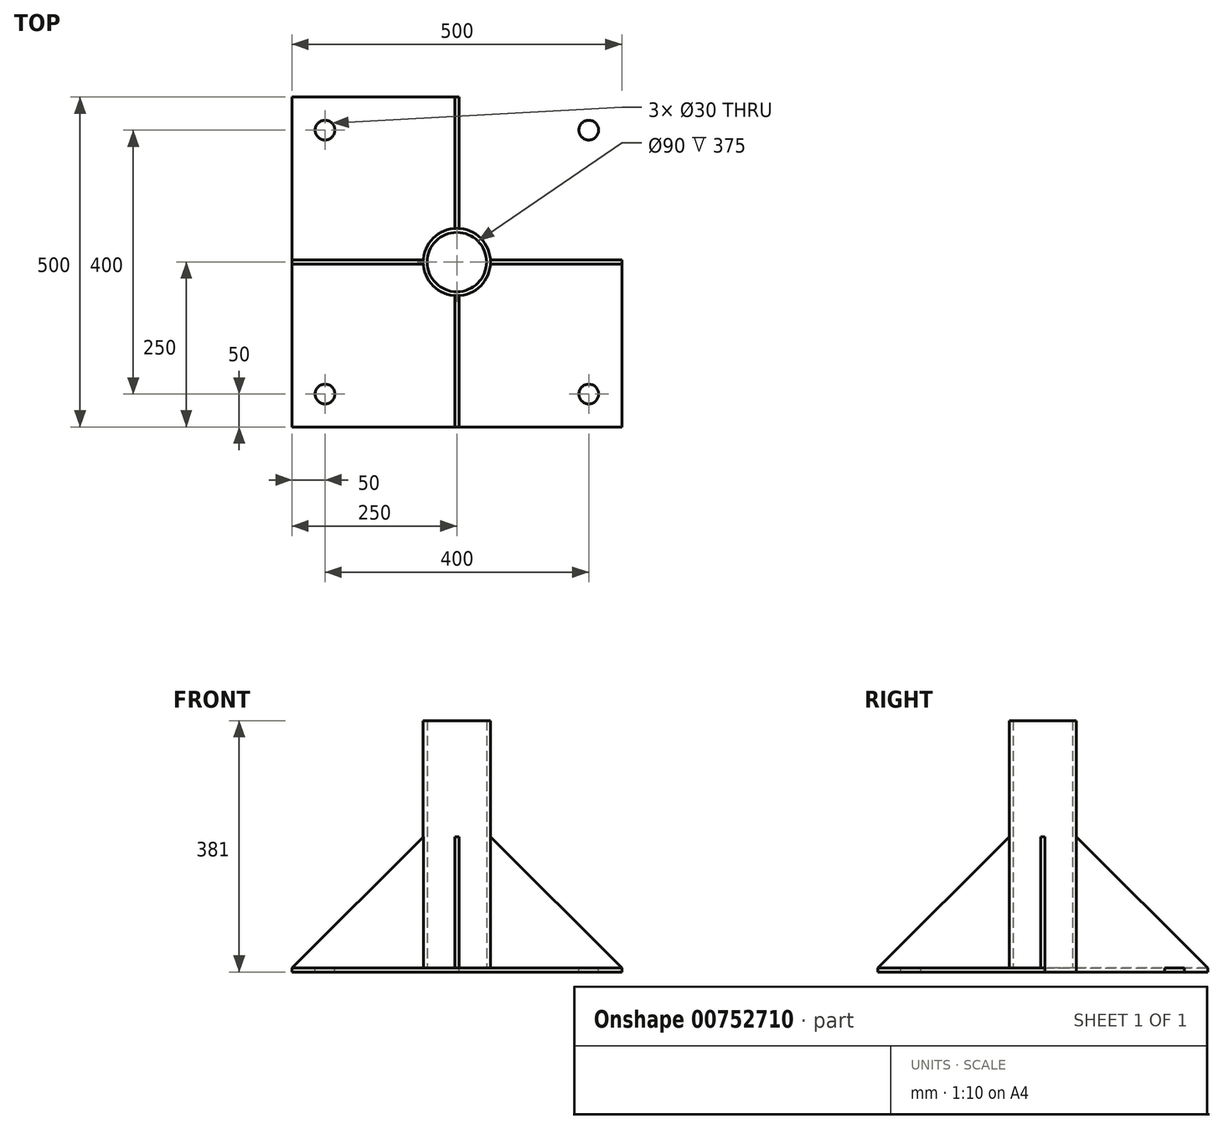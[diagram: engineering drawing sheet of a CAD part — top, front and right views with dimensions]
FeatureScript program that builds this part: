
annotation { "Feature Type Name" : "Feature", "Feature Type Description" : "" }
export const myFeature = defineFeature(function(context is Context, id is Id, definition is map)
    precondition{}
    {
        {
            var Q0;
            Q0=qCreatedBy(makeId("Top.planeOp"),FACE);
            var sketch = newSketch(context, id + "F0", { "sketchPlane" : qUnion([Q0])});
            skLineSegment(sketch, "E0.bottom", {"start": v(250, -250) * mm, "end": v(-250, -250) * mm});
            skLineSegment(sketch, "E0.top", {"start": v(250, 250) * mm, "end": v(-250, 250) * mm});
            skLineSegment(sketch, "E0.left", {"start": v(250, -250) * mm, "end": v(250, 250) * mm});
            skLineSegment(sketch, "E0.right", {"start": v(-250, -250) * mm, "end": v(-250, 250) * mm});
            skPoint(sketch, "E0.middle", {"position": v(0, 0) * mm});
            skSolve(sketch);
        }
        {
            var Q0;
            Q0=makeQuery(id+"F0.imprint","IMPRINT",FACE,{"disambiguationData":[TD([[makeQuery(id+"F0.imprint","IMPRINT",EDGE,{"derivedFrom":sQuery(id+"F0.wireOp",EDGE,"E0.bottom")}),-1.0]])]});
            extrude(context, id + "F1", {"entities" : qUnion([Q0]), "depth" : 6 * mm, "offsetDistance" : 25 * mm});
        }
        {
            var Q0;
            Q0=makeQuery(id+"F1.opExtrude","CAP_FACE",FACE,{"disambiguationData":[OSD([sQuery(id+"F0.wireOp",EDGE,"E0.bottom"),sQuery(id+"F0.wireOp",EDGE,"E0.top"),sQuery(id+"F0.wireOp",EDGE,"E0.left"),sQuery(id+"F0.wireOp",EDGE,"E0.right")])],"isStart":false});
            var sketch = newSketch(context, id + "F2", { "sketchPlane" : qUnion([Q0])});
            skCircle(sketch, "E1", {"center": v(0, 0) * mm, "radius": 45 * mm});
            skCircle(sketch, "E2", {"center": v(0, 0) * mm, "radius": 51 * mm});
            skLineSegment(sketch, "E3", {"start": v(250, 3) * mm, "end": v(50.91, 3) * mm});
            skLineSegment(sketch, "E4", {"start": v(250, -3) * mm, "end": v(50.91, -3) * mm});
            skLineSegment(sketch, "E5", {"start": v(-3, 250) * mm, "end": v(-3, 50.91) * mm});
            skLineSegment(sketch, "E6", {"start": v(3, 250) * mm, "end": v(3, 50.91) * mm});
            skLineSegment(sketch, "E7", {"start": v(3, -250) * mm, "end": v(3, -50.91) * mm});
            skLineSegment(sketch, "E8", {"start": v(-3, -250) * mm, "end": v(-3, -50.91) * mm});
            skLineSegment(sketch, "E9", {"start": v(-250, 3) * mm, "end": v(-50.91, 3) * mm});
            skLineSegment(sketch, "E10", {"start": v(-50.91, -3) * mm, "end": v(-250, -3) * mm});
            skCircle(sketch, "E11", {"center": v(200, 200) * mm, "radius": 15 * mm});
            skPoint(sketch, "E11.first.point", {"position": v(202.47, 214.8) * mm});
            skPoint(sketch, "E11.second.point", {"position": v(214.93, 198.54) * mm});
            skPoint(sketch, "E11.third.point", {"position": v(214.73, 197.19) * mm});
            skCircle(sketch, "E12", {"center": v(-200, 200) * mm, "radius": 15 * mm});
            skPoint(sketch, "E12.first.point", {"position": v(-187.4, 191.86) * mm});
            skPoint(sketch, "E12.second.point", {"position": v(-187.04, 207.55) * mm});
            skPoint(sketch, "E12.third.point", {"position": v(-185.27, 197.19) * mm});
            skCircle(sketch, "E13", {"center": v(-200, -200) * mm, "radius": 15 * mm});
            skPoint(sketch, "E13.first.point", {"position": v(-207.7, -212.87) * mm});
            skPoint(sketch, "E13.second.point", {"position": v(-194.3, -186.13) * mm});
            skPoint(sketch, "E13.third.point", {"position": v(-185.56, -204.06) * mm});
            skCircle(sketch, "E14", {"center": v(200, -200) * mm, "radius": 15 * mm});
            skPoint(sketch, "E14.first.point", {"position": v(186.75, -207.04) * mm});
            skPoint(sketch, "E14.second.point", {"position": v(214.73, -197.19) * mm});
            skPoint(sketch, "E14.third.point", {"position": v(193.26, -186.6) * mm});
            skSolve(sketch);
        }
        {
            var Q0;
            {var subQ0=sQuery(id+"F2.wireOp",EDGE,"E5");Q0=makeQuery(id+"F2.imprint","IMPRINT",FACE,{"disambiguationData":[TD([[makeQuery(id+"F2.imprint","IMPRINT",EDGE,{"derivedFrom":subQ0}),1.0]])]});}
            var Q1;
            {var subQ0=sQuery(id+"F2.wireOp",EDGE,"E3");Q1=makeQuery(id+"F2.imprint","IMPRINT",FACE,{"disambiguationData":[TD([[makeQuery(id+"F2.imprint","IMPRINT",EDGE,{"derivedFrom":subQ0}),1.0]])]});}
            var Q2;
            {var subQ0=sQuery(id+"F2.wireOp",EDGE,"E9");Q2=makeQuery(id+"F2.imprint","IMPRINT",FACE,{"disambiguationData":[TD([[makeQuery(id+"F2.imprint","IMPRINT",EDGE,{"derivedFrom":subQ0}),-1.0]])]});}
            var Q3;
            {var subQ0=sQuery(id+"F2.wireOp",EDGE,"E7");Q3=makeQuery(id+"F2.imprint","IMPRINT",FACE,{"disambiguationData":[TD([[makeQuery(id+"F2.imprint","IMPRINT",EDGE,{"derivedFrom":subQ0}),1.0]])]});}
            extrude(context, id + "F3", {"entities" : qUnion([Q0, Q1, Q2, Q3]), "operationType" : NewBodyOperationType.ADD, "depth" : 200.1 * mm, "offsetDistance" : 25 * mm});
        }
        {
            var Q0;
            Q0=makeQuery(id+"F3.opExtrude","SWEPT_FACE",FACE,{"disambiguationData":[OSD([sQuery(id+"F2.wireOp",EDGE,"E3")])]});
            var sketch = newSketch(context, id + "F4", { "sketchPlane" : qUnion([Q0])});
            skLineSegment(sketch, "E15", {"start": v(-250, 6) * mm, "end": v(-50.91, 205.09) * mm});
            skSolve(sketch);
        }
        {
            var Q0;
            {var subQ0=sQuery(id+"F4.wireOp",EDGE,"E15");Q0=makeQuery(id+"F4.imprint","IMPRINT",FACE,{"disambiguationData":[TD([[makeQuery(id+"F4.imprint","IMPRINT",EDGE,{"derivedFrom":subQ0}),1.0]])]});}
            extrude(context, id + "F5", {"entities" : qUnion([Q0]), "operationType" : NewBodyOperationType.REMOVE, "oppositeDirection" : true, "depth" : 25 * mm, "offsetDistance" : 25 * mm});
        }
        {
            var Q0;
            Q0=makeQuery(id+"F3.opExtrude","SWEPT_FACE",FACE,{"disambiguationData":[OSD([sQuery(id+"F2.wireOp",EDGE,"E7")])]});
            var sketch = newSketch(context, id + "F6", { "sketchPlane" : qUnion([Q0])});
            skLineSegment(sketch, "E16", {"start": v(-250, 6) * mm, "end": v(-50.91, 205.09) * mm});
            skSolve(sketch);
        }
        {
            var Q0;
            Q0=makeQuery(id+"F3.opExtrude","SWEPT_FACE",FACE,{"disambiguationData":[OSD([sQuery(id+"F2.wireOp",EDGE,"E5")])]});
            var sketch = newSketch(context, id + "F7", { "sketchPlane" : qUnion([Q0])});
            skLineSegment(sketch, "E17", {"start": v(-250, 6) * mm, "end": v(-50.91, 205.09) * mm});
            skSolve(sketch);
        }
        {
            var Q0;
            {var subQ0=sQuery(id+"F6.wireOp",EDGE,"E16");Q0=makeQuery(id+"F6.imprint","IMPRINT",FACE,{"disambiguationData":[TD([[makeQuery(id+"F6.imprint","IMPRINT",EDGE,{"derivedFrom":subQ0}),1.0]])]});}
            extrude(context, id + "F8", {"entities" : qUnion([Q0]), "operationType" : NewBodyOperationType.REMOVE, "oppositeDirection" : true, "depth" : 25 * mm, "offsetDistance" : 25 * mm});
        }
        {
            var Q0;
            {var subQ0=sQuery(id+"F7.wireOp",EDGE,"E17");Q0=makeQuery(id+"F7.imprint","IMPRINT",FACE,{"disambiguationData":[TD([[makeQuery(id+"F7.imprint","IMPRINT",EDGE,{"derivedFrom":subQ0}),1.0]])]});}
            extrude(context, id + "F9", {"entities" : qUnion([Q0]), "operationType" : NewBodyOperationType.REMOVE, "oppositeDirection" : true, "depth" : 25 * mm, "offsetDistance" : 25 * mm});
        }
        {
            var Q0;
            Q0=makeQuery(id+"F2.imprint","IMPRINT",FACE,{"disambiguationData":[TD([[makeQuery(id+"F2.imprint","IMPRINT",EDGE,{"derivedFrom":sQuery(id+"F2.wireOp",EDGE,"E13")}),1.0]])]});
            var Q1;
            Q1=makeQuery(id+"F2.imprint","IMPRINT",FACE,{"disambiguationData":[TD([[makeQuery(id+"F2.imprint","IMPRINT",EDGE,{"derivedFrom":sQuery(id+"F2.wireOp",EDGE,"E14")}),1.0]])]});
            var Q2;
            Q2=makeQuery(id+"F2.imprint","IMPRINT",FACE,{"disambiguationData":[TD([[makeQuery(id+"F2.imprint","IMPRINT",EDGE,{"derivedFrom":sQuery(id+"F2.wireOp",EDGE,"E11")}),-1.0]])]});
            var Q3;
            Q3=makeQuery(id+"F2.imprint","IMPRINT",FACE,{"disambiguationData":[TD([[makeQuery(id+"F2.imprint","IMPRINT",EDGE,{"derivedFrom":sQuery(id+"F2.wireOp",EDGE,"E12")}),1.0]])]});
            extrude(context, id + "F10", {"entities" : qUnion([Q0, Q1, Q2, Q3]), "operationType" : NewBodyOperationType.REMOVE, "oppositeDirection" : true, "depth" : 25 * mm, "offsetDistance" : 25 * mm});
        }
        {
            var Q0;
            Q0=makeQuery(id+"F3.opExtrude","SWEPT_FACE",FACE,{"disambiguationData":[OSD([sQuery(id+"F2.wireOp",EDGE,"E10")])]});
            var sketch = newSketch(context, id + "F11", { "sketchPlane" : qUnion([Q0])});
            skLineSegment(sketch, "E18", {"start": v(-250, 6) * mm, "end": v(-50.91, 205.09) * mm});
            skSolve(sketch);
        }
        {
            var Q0;
            {var subQ0=sQuery(id+"F11.wireOp",EDGE,"E18");Q0=makeQuery(id+"F11.imprint","IMPRINT",FACE,{"disambiguationData":[TD([[makeQuery(id+"F11.imprint","IMPRINT",EDGE,{"derivedFrom":subQ0}),1.0]])]});}
            extrude(context, id + "F12", {"entities" : qUnion([Q0]), "operationType" : NewBodyOperationType.REMOVE, "oppositeDirection" : true, "depth" : 25 * mm, "offsetDistance" : 25 * mm});
        }
        {
            var Q0;
            Q0=makeQuery(id+"F2.imprint","IMPRINT",FACE,{"disambiguationData":[TD([[makeQuery(id+"F2.imprint","IMPRINT",EDGE,{"derivedFrom":sQuery(id+"F2.wireOp",EDGE,"E1")}),-1.0]])]});
            extrude(context, id + "F13", {"entities" : qUnion([Q0]), "operationType" : NewBodyOperationType.ADD, "depth" : 375 * mm, "offsetDistance" : 25 * mm});
        }
    });
